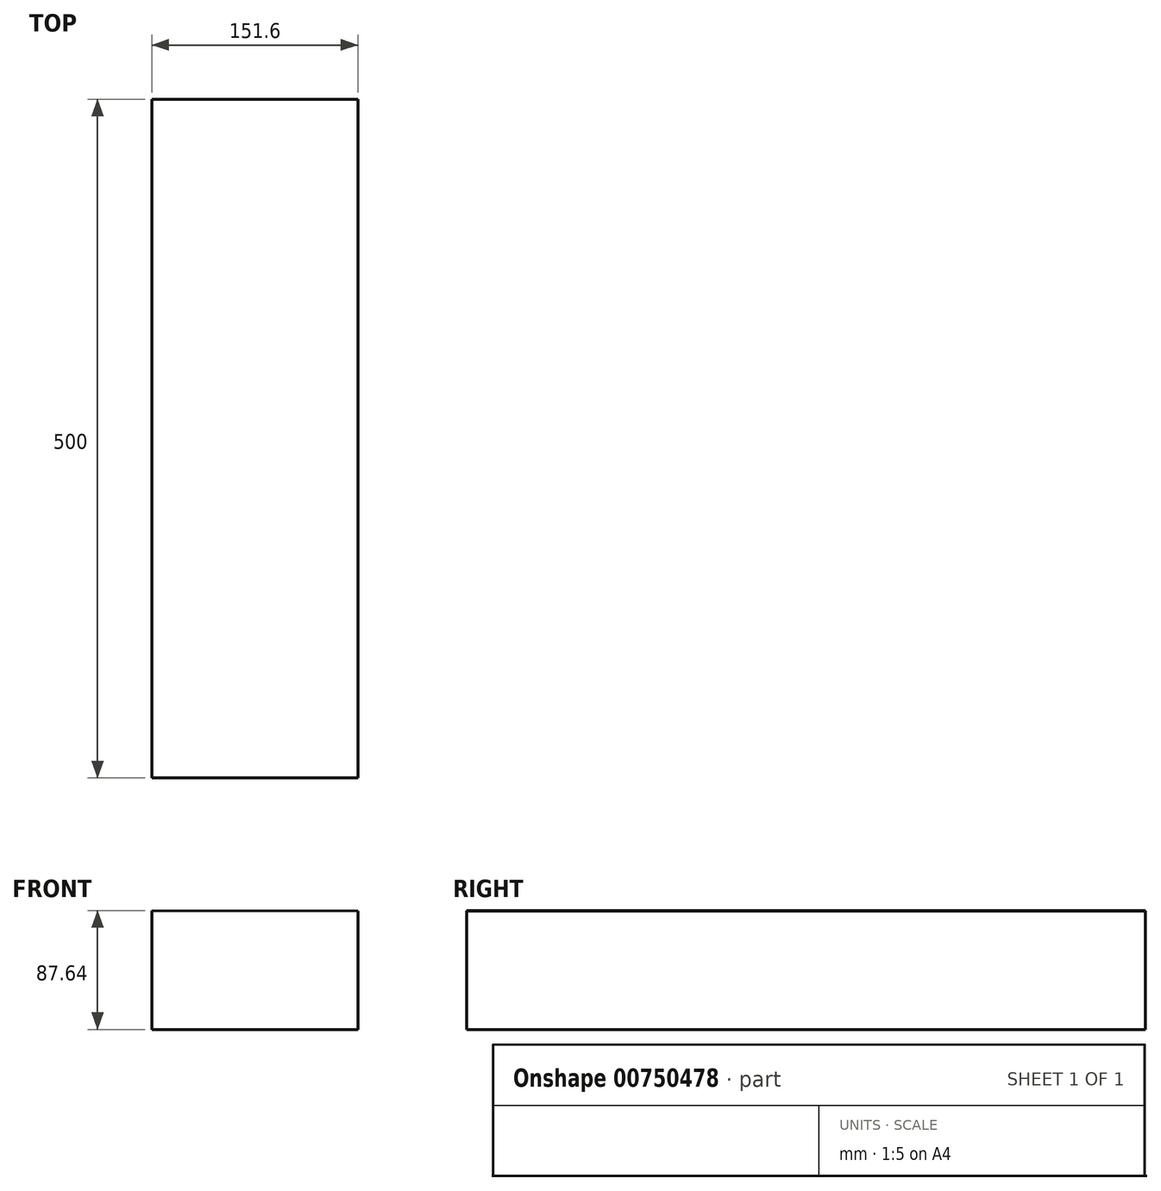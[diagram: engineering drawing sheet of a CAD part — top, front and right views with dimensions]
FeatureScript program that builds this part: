
annotation { "Feature Type Name" : "Feature", "Feature Type Description" : "" }
export const myFeature = defineFeature(function(context is Context, id is Id, definition is map)
    precondition{}
    {
        {
            var Q0;
            Q0=qCreatedBy(makeId("Front.planeOp"),FACE);
            var sketch = newSketch(context, id + "F0", { "sketchPlane" : qUnion([Q0])});
            skLineSegment(sketch, "E0", {"start": v(-75.37, 14.86) * mm, "end": v(-75.37, -72.78) * mm});
            skLineSegment(sketch, "E1", {"start": v(-75.37, -72.78) * mm, "end": v(76.23, -72.78) * mm});
            skLineSegment(sketch, "E2", {"start": v(76.23, -72.78) * mm, "end": v(76.23, 14.35) * mm});
            skLineSegment(sketch, "E3", {"start": v(-75.37, 14.86) * mm, "end": v(76.23, 14.35) * mm});
            skSolve(sketch);
        }
        {
            var Q0;
            Q0 = qSketchRegion(id + "F0", true);
            extrude(context, id + "F1", {"entities" : qUnion([Q0]), "depth" : 500 * mm, "offsetDistance" : 25.4 * mm});
        }
    });
